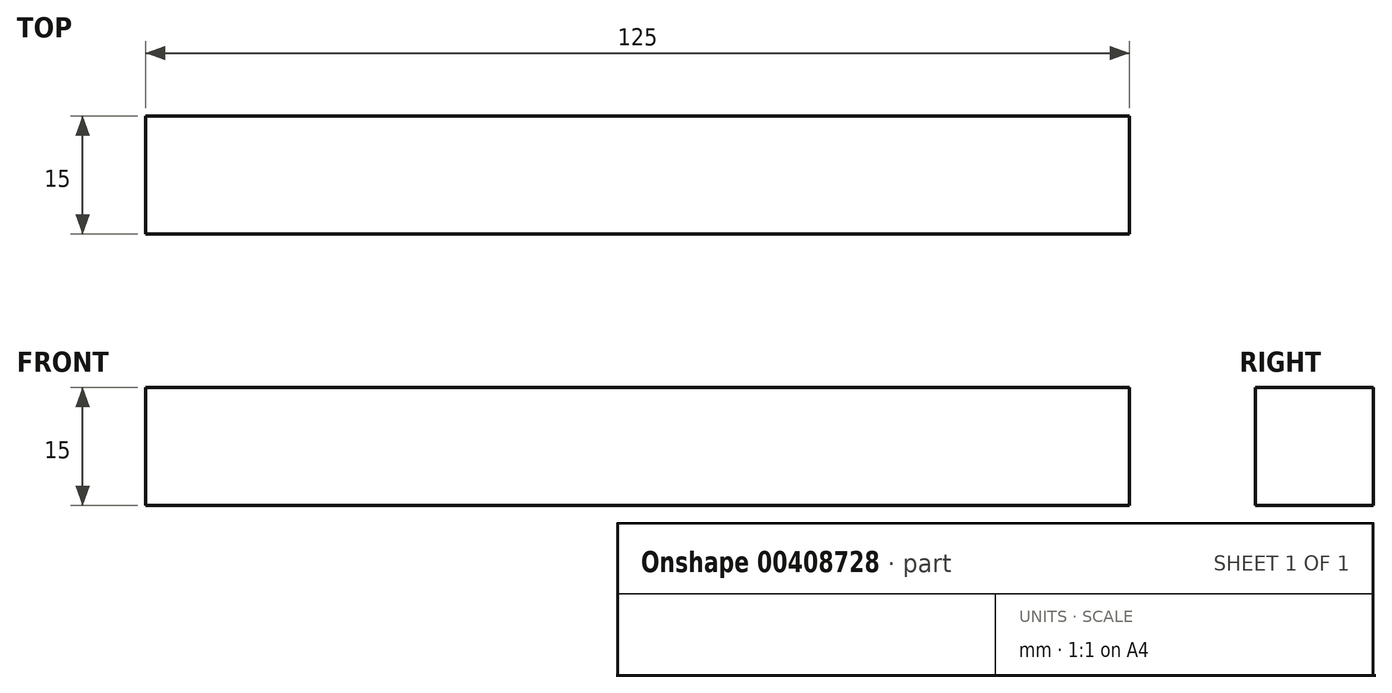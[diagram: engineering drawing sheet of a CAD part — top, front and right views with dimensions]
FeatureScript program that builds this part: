
annotation { "Feature Type Name" : "Feature", "Feature Type Description" : "" }
export const myFeature = defineFeature(function(context is Context, id is Id, definition is map)
    precondition{}
    {
        {
            var Q0;
            Q0=qCreatedBy(makeId("Top.planeOp"),FACE);
            var sketch = newSketch(context, id + "F0", { "sketchPlane" : qUnion([Q0])});
            skLineSegment(sketch, "E0.bottom", {"start": v(-62.5, 7.5) * mm, "end": v(62.5, 7.5) * mm});
            skLineSegment(sketch, "E0.top", {"start": v(-62.5, -7.5) * mm, "end": v(62.5, -7.5) * mm});
            skLineSegment(sketch, "E0.left", {"start": v(-62.5, 7.5) * mm, "end": v(-62.5, -7.5) * mm});
            skLineSegment(sketch, "E0.right", {"start": v(62.5, 7.5) * mm, "end": v(62.5, -7.5) * mm});
            skPoint(sketch, "E0.middle", {"position": v(0, 0) * mm});
            skSolve(sketch);
        }
        {
            var Q0;
            Q0 = qSketchRegion(id + "F0", true);
            extrude(context, id + "F1", {"entities" : qUnion([Q0]), "depth" : 15 * mm});
        }
    });
